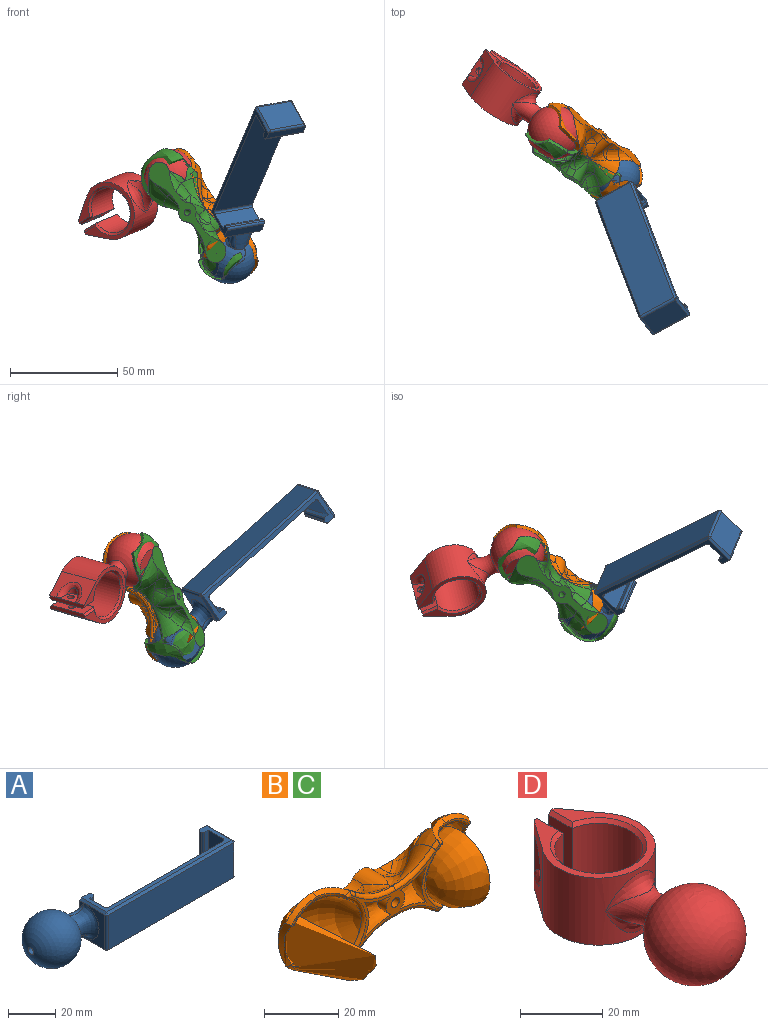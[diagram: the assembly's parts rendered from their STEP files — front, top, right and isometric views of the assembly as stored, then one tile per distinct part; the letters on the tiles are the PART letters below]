
ASSEMBLY  parts=4 mates=4
PART A: 46 faces, bbox 109.4x26.9x25.9 mm
  f0: plane 18.06x12.56mm, normal (-1,0,0), area 97.7mm2, adj f19,f29,f36,f45
  f1: plane 5.66x3.37mm, normal (-1,0,0), area 4.8mm2, adj f8,f20,f45
  f2: sphere r=12.5mm, area 1668.1mm2, adj f3,f18,f19,f20,f21,f22
  f3: plane 15x15mm, normal (0,0,-1), area 176.7mm2, adj f2
  f4: plane 5.66x3.37mm, normal (-1,0,0), area 4.8mm2, adj f8,f21,f36
  f5: plane 20x9mm, normal (1,0,0), area 180mm2, adj f6,f16,f17,f35
  f6: plane 20x2mm, normal (0,-1,0), area 40mm2, adj f5,f16,f17,f27
  f7: plane 20x1mm, normal (1,0,0), area 20mm2, adj f16,f17,f27,f28
  f8: plane 20x5mm, normal (0,1,0), area 99mm2, adj f1,f4,f16,f17,f18,f28,f36,f45
  f9: plane 74.75x18mm, normal (0,-1,0), area 1345.5mm2, adj f29,f30,f38,f43
  f10: plane 18x14mm, normal (1,0,0), area 252mm2, adj f30,f31,f40,f41
  f11: plane 20x4mm, normal (0,1,0), area 80mm2, adj f16,f17,f31,f32
  f12: plane 20x1mm, normal (-1,0,0), area 20mm2, adj f16,f17,f32,f33
  f13: plane 20x2mm, normal (0,-1,0), area 40mm2, adj f14,f16,f17,f33
  f14: plane 20x9mm, normal (-1,0,0), area 180mm2, adj f13,f16,f17,f34
  f15: plane 68.75x20mm, normal (0,1,0), area 1375mm2, adj f16,f17,f34,f35
  f16: plane 74.75x15mm, normal (0,0,1), area 219.1mm2, adj f5,f6,f7,f8,f11,f12,f13,f14
  f17: plane 74.75x15mm, normal (0,0,-1), area 219.1mm2, adj f5,f6,f7,f8,f11,f12,f13,f14
  f18: bspline ~14.32x8mm, area 52.9mm2, adj f2,f8,f20,f21
  f19: bspline ~18x13.55mm, area 213.3mm2, adj f0,f2,f20,f21
  f20: bspline ~11.31x8.33mm, area 31.4mm2, adj f1,f2,f18,f19
  f21: bspline ~11.31x8.33mm, area 31.4mm2, adj f2,f4,f18,f19
  f22: cone r=1.62mm half-angle=3deg, axis (-1,0,0), area 33.7mm2, adj f2,f23
  f23: sphere r=9mm, area 804.6mm2, adj f22,f24,f25
  f24: plane 8.83x8.83mm, normal (-1,0,0), area 60.2mm2, adj f23,f26
  f25: plane 12.45x12.45mm, normal (0,0,1), area 121.7mm2, adj f23
  f26: cone r=1.62mm half-angle=3deg, axis (-1,0,0), area 18.7mm2, adj f24
  f27: cylinder r=1mm len=20mm, axis (0,0,1), area 31.4mm2, adj f6,f7,f16,f17
  f28: cylinder r=1mm len=20mm, axis (0,0,-1), area 31.4mm2, adj f7,f8,f16,f17
  f29: cylinder r=1mm len=18mm, axis (0,0,-1), area 28.3mm2, adj f0,f9,f37,f44
  f30: cylinder r=1mm len=18mm, axis (0,0,-1), area 28.3mm2, adj f9,f10,f39,f42
  f31: cylinder r=1mm len=20mm, axis (0,0,-1), area 29.8mm2, adj f10,f11,f40,f41
  f32: cylinder r=1mm len=20mm, axis (0,0,-1), area 31.4mm2, adj f11,f12,f16,f17
  f33: cylinder r=1mm len=20mm, axis (0,0,1), area 31.4mm2, adj f12,f13,f16,f17
  f34: cylinder r=1mm len=20mm, axis (0,0,1), area 31.4mm2, adj f14,f15,f16,f17
  f35: cylinder r=1mm len=20mm, axis (0,0,1), area 31.4mm2, adj f5,f15,f16,f17
  f36: plane 15x1mm, normal (-0.71,0,0.71), area 21.2mm2, adj f0,f4,f8,f16,f37
  f37: cone r=1mm half-angle=45deg, axis (0,0,-1), area 1.1mm2, adj f29,f36,f38
  f38: plane 74.75x1mm, normal (0,-0.71,0.71), area 105.7mm2, adj f9,f16,f37,f39
  f39: cone r=1mm half-angle=45deg, axis (0,0,-1), area 1.1mm2, adj f30,f38,f40
  f40: plane 15.42x1.42mm, normal (0.71,0,0.71), area 20.9mm2, adj f10,f16,f31,f39
  f41: plane 15.42x1.42mm, normal (0.71,0,-0.71), area 20.9mm2, adj f10,f17,f31,f42
  f42: cone r=1mm half-angle=45deg, axis (0,0,1), area 1.1mm2, adj f30,f41,f43
  f43: plane 74.75x1mm, normal (0,-0.71,-0.71), area 105.7mm2, adj f9,f17,f42,f44
  f44: cone r=1mm half-angle=45deg, axis (0,0,1), area 1.1mm2, adj f29,f43,f45
  f45: plane 15x1mm, normal (-0.71,0,-0.71), area 21.2mm2, adj f0,f1,f8,f17,f44
PART B: 91 faces, bbox 72.1x19x28.1 mm
  f0: plane 59.78x10.4mm, normal (0,1,0), area 350.5mm2, adj f1,f2,f7,f13,f14,f15,f21,f23
  f1: plane 4.98x3.76mm, normal (0,0,1), area 10.1mm2, adj f0,f21,f22,f23
  f2: plane 4.98x3.76mm, normal (0,0,-1), area 10.1mm2, adj f0,f26,f27,f28
  f3: revolved ~14.78x8.77mm, area 71.8mm2, adj f7,f26,f28,f30,f44,f87
  f4: plane 9.69x5.17mm, normal (0,-1,0), area 6.9mm2, adj f10,f12,f33,f34,f39
  f5: revolved ~22.89x20.47mm, area 471.5mm2, adj f36,f37,f38,f39,f40,f41
  f6: revolved ~14.78x8.77mm, area 71.8mm2, adj f7,f21,f22,f25,f47,f81
  f7: revolved ~27.88x20.27mm, area 464.7mm2, adj f0,f3,f6,f21,f26,f31,f32,f33
  f8: plane 34.91x21.57mm, normal (0,-1,0), area 121.4mm2, adj f15,f16,f17,f18,f19,f20,f36,f53
  f9: plane 9.69x5.17mm, normal (0,-1,0), area 6.9mm2, adj f11,f12,f32,f33,f40
  f10: cylinder r=6.5mm len=6.41mm, axis (0,0,1), area 5.7mm2, adj f4,f35,f36,f37,f79
  f11: cylinder r=6.5mm len=6.41mm, axis (0,0,1), area 5.7mm2, adj f9,f31,f36,f38,f85
  f12: cylinder r=9mm len=12.45mm, axis (1,0,0), area 11.1mm2, adj f4,f9,f33,f39,f40,f41
  f13: cylinder r=4.5mm len=9.88mm, axis (0,1,0), area 50.1mm2, adj f0,f27,f30,f64,f67
  f14: cylinder r=4.5mm len=9.88mm, axis (0,1,0), area 50.1mm2, adj f0,f23,f25,f60,f62
  f15: cylinder r=1.5mm len=13mm, axis (0,1,0), area 122.5mm2, adj f0,f8
  f16: cylinder r=3.5mm len=5.74mm, axis (0,1,0), area 17mm2, adj f8,f17,f19,f20
  f17: plane 1.05x0.19mm, normal (-1,0,0), area 0.1mm2, adj f8,f16,f20
  f18: revolved ~11.81x5.9mm, area 58.7mm2, adj f8,f20
  f19: plane 1.05x0.19mm, normal (-1,0,0), area 0.1mm2, adj f8,f16,f20
  f20: revolved ~11.81x9.75mm, area 125.1mm2, adj f8,f16,f17,f18,f19
  f21: bspline ~12.49x9.13mm, area 25.5mm2, adj f0,f1,f6,f7,f22
  f22: bspline ~9.56x8.32mm, area 36.1mm2, adj f1,f6,f21,f24
  f23: cylinder r=5mm len=3.75mm, axis (0,1,0), area 15.3mm2, adj f0,f1,f14,f24
  f24: sphere r=5mm, area 20.4mm2, adj f22,f23,f25
  f25: bspline ~10.34x8.54mm, area 33.7mm2, adj f6,f14,f24,f62
  f26: bspline ~13.1x9.66mm, area 25.5mm2, adj f0,f2,f3,f7,f28
  f27: cylinder r=5mm len=3.75mm, axis (0,1,0), area 15.3mm2, adj f0,f2,f13,f29
  f28: bspline ~9.56x8.32mm, area 36.1mm2, adj f2,f3,f26,f29
  f29: sphere r=5mm, area 20.4mm2, adj f27,f28,f30
  f30: bspline ~9.38x7.96mm, area 33.7mm2, adj f3,f13,f29,f67
  f31: bspline ~7.76x6.42mm, area 16mm2, adj f7,f11,f32,f85,f86
  f32: bspline ~11.42x7.33mm, area 19.3mm2, adj f7,f9,f31,f33
  f33: bspline ~15.24x4.31mm, area 27mm2, adj f4,f7,f9,f12,f32,f34
  f34: bspline ~11.42x7.33mm, area 19.3mm2, adj f4,f7,f33,f35
  f35: bspline ~7.76x6.42mm, area 16mm2, adj f7,f10,f34,f79,f80
  f36: bspline ~21.95x7.72mm, area 36.2mm2, adj f5,f8,f10,f11,f37,f38,f79,f85
  f37: bspline ~8.5x6.98mm, area 9.1mm2, adj f5,f10,f36,f39
  f38: bspline ~8.5x6.98mm, area 9.1mm2, adj f5,f11,f36,f40
  f39: bspline ~10.93x5.33mm, area 10mm2, adj f4,f5,f12,f37,f41
  f40: bspline ~10.93x5.33mm, area 10mm2, adj f5,f9,f12,f38,f41
  f41: bspline ~14.29x3.88mm, area 9.7mm2, adj f5,f12,f39,f40
  f42: plane 4.98x3.76mm, normal (0,0,1), area 10.1mm2, adj f0,f58,f59,f60
  f43: plane 4.98x3.76mm, normal (0,0,-1), area 10.1mm2, adj f0,f63,f64,f65
  f44: revolved ~14.78x8.77mm, area 71.8mm2, adj f3,f48,f63,f65,f67,f88
  f45: plane 9.69x5.17mm, normal (0,-1,0), area 6.9mm2, adj f50,f52,f70,f71,f76
  f46: revolved ~22.89x20.47mm, area 471.5mm2, adj f73,f74,f75,f76,f77,f78
  f47: revolved ~14.78x8.77mm, area 71.8mm2, adj f6,f48,f58,f59,f62,f82
  f48: revolved ~27.88x20.27mm, area 464.6mm2, adj f0,f44,f47,f58,f63,f68,f69,f70
  f49: plane 9.69x5.17mm, normal (0,-1,0), area 6.9mm2, adj f51,f52,f69,f70,f77
  f50: cylinder r=6.5mm len=6.41mm, axis (0,0,1), area 5.7mm2, adj f45,f72,f73,f74,f83
  f51: cylinder r=6.5mm len=6.41mm, axis (0,0,1), area 5.7mm2, adj f49,f68,f73,f75,f90
  f52: cylinder r=9mm len=12.45mm, axis (-1,0,0), area 11.1mm2, adj f45,f49,f70,f76,f77,f78
  f53: cylinder r=3.5mm len=5.74mm, axis (0,1,0), area 17mm2, adj f8,f54,f56,f57
  f54: plane 1.05x0.19mm, normal (1,0,0), area 0.1mm2, adj f8,f53,f57
  f55: revolved ~11.81x5.9mm, area 58.7mm2, adj f8,f57
  f56: plane 1.05x0.19mm, normal (1,0,0), area 0.1mm2, adj f8,f53,f57
  f57: revolved ~11.81x9.75mm, area 125.1mm2, adj f8,f53,f54,f55,f56
  f58: bspline ~13.1x9.66mm, area 25.5mm2, adj f0,f42,f47,f48,f59
  f59: bspline ~9.56x8.32mm, area 36.1mm2, adj f42,f47,f58,f61
  f60: cylinder r=5mm len=3.75mm, axis (0,1,0), area 15.3mm2, adj f0,f14,f42,f61
  f61: sphere r=5mm, area 16.3mm2, adj f59,f60,f62
  f62: bspline ~10.05x8.54mm, area 33.7mm2, adj f14,f25,f47,f61
  f63: bspline ~12.49x9.13mm, area 25.5mm2, adj f0,f43,f44,f48,f65
  f64: cylinder r=5mm len=3.75mm, axis (0,1,0), area 15.3mm2, adj f0,f13,f43,f66
  f65: bspline ~9.56x8.32mm, area 36.1mm2, adj f43,f44,f63,f66
  f66: sphere r=5mm, area 20.4mm2, adj f64,f65,f67
  f67: bspline ~9.72x7.96mm, area 33.7mm2, adj f13,f30,f44,f66
  f68: bspline ~7.97x7.55mm, area 16mm2, adj f48,f51,f69,f89,f90
  f69: bspline ~11.42x7.33mm, area 19.3mm2, adj f48,f49,f68,f70
  f70: bspline ~15.99x4.66mm, area 27mm2, adj f45,f48,f49,f52,f69,f71
  f71: bspline ~10.29x5.59mm, area 19.3mm2, adj f45,f48,f70,f72
  f72: bspline ~7.76x6.42mm, area 16mm2, adj f48,f50,f71,f83,f84
  f73: bspline ~21.95x7.72mm, area 36.2mm2, adj f8,f46,f50,f51,f74,f75,f83,f90
  f74: bspline ~8.5x6.98mm, area 9.1mm2, adj f46,f50,f73,f76
  f75: bspline ~8.5x6.98mm, area 9.1mm2, adj f46,f51,f73,f77
  f76: bspline ~10.93x5.33mm, area 10mm2, adj f45,f46,f52,f74,f78
  f77: bspline ~10.93x5.33mm, area 10mm2, adj f46,f49,f52,f75,f78
  f78: bspline ~14.29x3.88mm, area 9.7mm2, adj f46,f52,f76,f77
  f79: bspline ~2.26x1.82mm, area 1.9mm2, adj f8,f10,f35,f36,f80
  f80: bspline ~3.63x3.01mm, area 3.6mm2, adj f7,f8,f35,f79,f81
  f81: bspline ~21.28x7mm, area 28.5mm2, adj f6,f7,f8,f80,f82
  f82: bspline ~21.28x7mm, area 28.5mm2, adj f8,f47,f48,f81,f84
  f83: bspline ~2.41x1.9mm, area 1.9mm2, adj f8,f50,f72,f73,f84
  f84: bspline ~3.63x3.01mm, area 3.6mm2, adj f8,f48,f72,f82,f83
  f85: bspline ~2.26x1.82mm, area 1.9mm2, adj f8,f11,f31,f36,f86
  f86: bspline ~3.63x3.01mm, area 3.6mm2, adj f7,f8,f31,f85,f87
  f87: bspline ~21.28x7mm, area 28.5mm2, adj f3,f7,f8,f86,f88
  f88: bspline ~21.28x7mm, area 28.5mm2, adj f8,f44,f48,f87,f89
  f89: bspline ~3.63x3.01mm, area 3.6mm2, adj f8,f48,f68,f88,f90
  f90: bspline ~2.41x1.9mm, area 1.9mm2, adj f8,f51,f68,f73,f89
PART C: same geometry as B
PART D: 32 faces, bbox 27.5x64.4x25 mm
  f0: cylinder r=13.75mm len=27.5mm, axis (0,0,-1), area 1205.2mm2, adj f1,f5,f6,f26,f27,f28
  f1: bspline ~16.85x8.55mm, area 0mm2, adj f0,f2
  f2: revolved ~16.85x16.85mm, area 232.1mm2, adj f1,f3,f5
  f3: sphere r=12.5mm, area 1676.4mm2, adj f2,f4
  f4: plane 15x15mm, normal (0,0,-1), area 176.7mm2, adj f3
  f5: bspline ~16.85x8.55mm, area 0mm2, adj f0,f2
  f6: plane 20x10.76mm, normal (-0.81,0.58,0), area 162.4mm2, adj f0,f7,f25,f26,f28
  f7: bspline ~12.5x8.2mm, area 68.7mm2, adj f6,f8,f9
  f8: cylinder r=3.25mm len=6.27mm, axis (1,0,0), area 0mm2, adj f7,f9
  f9: plane 12x6.75mm, normal (-1,0,0), area 37mm2, adj f7,f8,f10,f25
  f10: cylinder r=1.62mm len=3.25mm, axis (1,0,0), area 20.4mm2, adj f9,f11
  f11: plane 18x8.11mm, normal (1,0,0), area 137.6mm2, adj f10,f12,f23,f24,f25
  f12: plane 8.14x1.03mm, normal (0.71,0,0.71), area 10.9mm2, adj f11,f13,f25,f26
  f13: cone r=10.75mm half-angle=45deg, axis (0,0,1), area 94.3mm2, adj f12,f14,f24,f26
  f14: plane 8.14x1.03mm, normal (-0.71,0,0.71), area 10.9mm2, adj f13,f15,f22,f26
  f15: plane 18x8.11mm, normal (-1,0,0), area 137.6mm2, adj f14,f16,f18,f22,f24
  f16: plane 8.14x1.03mm, normal (-0.71,0,-0.71), area 10.9mm2, adj f15,f17,f22,f28
  f17: cone r=11.75mm half-angle=45deg, axis (0,0,-1), area 94.3mm2, adj f16,f23,f24,f28
  f18: cylinder r=1.62mm len=3.25mm, axis (1,0,0), area 20.4mm2, adj f15,f19
  f19: plane 12x6.75mm, normal (1,0,0), area 37mm2, adj f18,f20,f21,f22
  f20: cylinder r=3.25mm len=6.27mm, axis (-1,0,0), area 0mm2, adj f19,f21
  f21: bspline ~12.5x8.2mm, area 68.7mm2, adj f19,f20,f27
  f22: plane 20x2mm, normal (0,1,0), area 39mm2, adj f14,f15,f16,f19,f26,f27,f28
  f23: plane 8.14x1.03mm, normal (0.71,0,-0.71), area 10.9mm2, adj f11,f17,f25,f28
  f24: cylinder r=10.75mm len=21.5mm, axis (0,0,-1), area 1161.6mm2, adj f11,f13,f15,f17
  f25: plane 20x2mm, normal (0,1,0), area 39mm2, adj f6,f9,f11,f12,f23,f26,f28
  f26: plane 32.5x27.5mm, normal (0,0,1), area 192.5mm2, adj f0,f6,f12,f13,f14,f22,f25,f27
  f27: plane 20x10.76mm, normal (0.81,0.58,0), area 162.4mm2, adj f0,f21,f22,f26,f28
  f28: plane 32.5x27.5mm, normal (0,0,-1), area 192.5mm2, adj f0,f6,f16,f17,f22,f23,f25,f27
  f29: sphere r=9mm, area 811.2mm2, adj f30,f31
  f30: plane 8.83x8.83mm, normal (0,-1,0), area 61.2mm2, adj f29
  f31: plane 12.45x12.45mm, normal (0,0,1), area 121.7mm2, adj f29
PLACE A rot(axis=(-0.73,0.14,-0.67),122.9deg) t=(-5.28,-52.34,-13.01)mm fixed
PLACE B rot(axis=(-0.36,-0.89,-0.28),140.7deg) t=(-25.61,-27.22,-9.15)mm
PLACE C rot(axis=(0.43,-0.03,0.9),152.3deg) t=(-24.41,-25.71,-9.08)mm
PLACE D rot(axis=(-0.62,0.72,0.31),81.8deg) t=(-61.46,2.76,-4.09)mm
MATE ball B.f3 <-> D.f3  axis (0.54,-0.4,-0.74) through (-38.53,-16.6,9.86)mm
MATE ball D.f3 <-> C.f3  axis (0.54,0.81,0.23) through (-38.53,-16.6,9.86)mm
MATE ball C.f57 <-> A.f2  axis (-0.54,0.4,0.74) through (-11.18,-36.59,-27.73)mm
MATE ball B.f57 <-> A.f2  axis (-0.54,0.4,0.74) through (-11.18,-36.59,-27.73)mm
